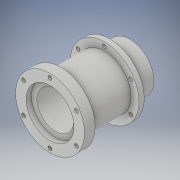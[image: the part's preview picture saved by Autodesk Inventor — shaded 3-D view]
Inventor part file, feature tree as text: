
AUTODESK INVENTOR PART (.ipt)
format: ipt  version: 2017 (Build 210142000, 142)  size: 167,936 bytes
history: native  units: in
note: dims shown in document units (in); Inventor stores cm internally (conversion verified against a paired STEP export)
features: extrude x7, sketch x7
ambient origin geometry x8: Origin, YZ Plane, XZ Plane, XY Plane, X Axis, Y Axis, Z Axis, Center Point
bodies: Solid1 (feature_tree)
feature tree (14):
  extrude  "Extrusion1"  Depth=3.76in TaperAngle=0.0deg
  extrude  "Extrusion2"  Depth=3.76in TaperAngle=0.0deg
  extrude  "Extrusion3"  Depth=0.95in TaperAngle=0.0deg
  extrude  "Extrusion4"  Depth=0.25in TaperAngle=0.0deg
  extrude  "Extrusion5"  Depth=2.56in TaperAngle=0.0deg
  extrude  "Extrusion6"  Depth=0.5in
  extrude  "Extrusion7"  Depth=6.0in TaperAngle=0.0deg
  sketch  "Sketch1"  dims[d0=3.24in d1=3.76in d2=0.0in]
  sketch  "Sketch2"  dims[d3=1.74in d4=3.76in d5=0.0in]
  sketch  "Sketch3"  dims[d6=2.25in d7=0.95in d8=0.0in]
  sketch  "Sketch4"  dims[d9=2.25in d10=0.25in d11=0.0in]
  sketch  "Sketch5"  dims[d12=2.5in d13=2.56in d14=0.0in]
  sketch  "Sketch6"  dims[d15=0.5in d16=0.0in d17=0.1875in]
  sketch  "Sketch7"  dims[d18=2.3622in d20=360.0deg d22=6.0in d23=0.0in]
